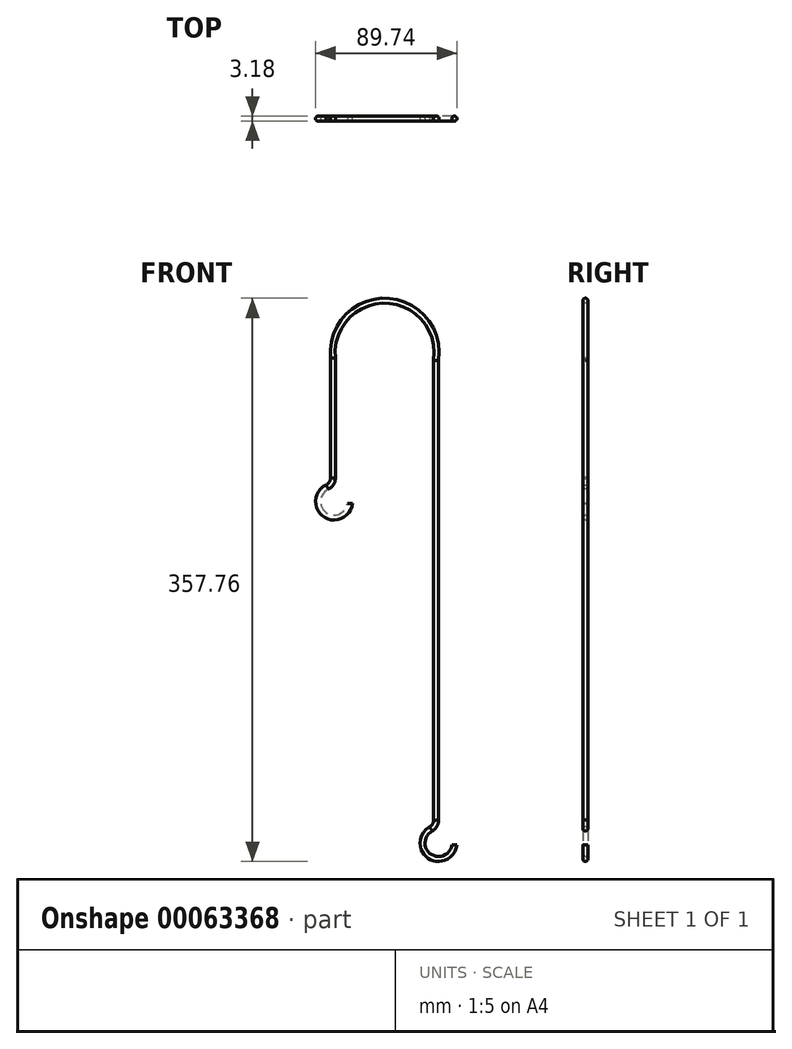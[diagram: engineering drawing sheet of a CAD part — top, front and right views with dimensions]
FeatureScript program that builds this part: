
annotation { "Feature Type Name" : "Feature", "Feature Type Description" : "" }
export const myFeature = defineFeature(function(context is Context, id is Id, definition is map)
    precondition{}
    {
        {
            var Q0;
            Q0=qCreatedBy(makeId("Front.planeOp"),FACE);
            var sketch = newSketch(context, id + "F0", { "sketchPlane" : qUnion([Q0])});
            skLineSegment(sketch, "E0", {"start": v(-32.84, 68.58) * mm, "end": v(-32.84, -7.62) * mm});
            skArc(sketch, "E1", {"start": v(32.66, 67.11) * mm, "mid": v(0.74, 105) * mm, "end": v(-32.84, 68.58) * mm});
            skLineSegment(sketch, "E2", {"start": v(32.66, 67.11) * mm, "end": v(32.66, -224.94) * mm});
            skArc(sketch, "E3", {"start": v(-36.48, -13.36) * mm, "mid": v(-38.06, -30.78) * mm, "end": v(-22.04, -23.75) * mm});
            skArc(sketch, "E4", {"start": v(29.34, -230.51) * mm, "mid": v(28.47, -247.82) * mm, "end": v(44.28, -240.74) * mm});
            skPoint(sketch, "E5.visualSharp", {"position": v(-32.84, -12.4) * mm});
            skArc(sketch, "E5.filletArc", {"start": v(-36.48, -13.36) * mm, "mid": v(-33.83, -11.01) * mm, "end": v(-32.84, -7.62) * mm});
            skPoint(sketch, "E6.visualSharp", {"position": v(32.66, -229.4) * mm});
            skArc(sketch, "E6.filletArc", {"start": v(29.34, -230.51) * mm, "mid": v(31.77, -228.18) * mm, "end": v(32.66, -224.94) * mm});
            skPoint(sketch, "E7", {"position": v(0, 105.02) * mm});
            skSolve(sketch);
        }
        {
            var Q0;
            Q0=sQuery(id+"F0.wireOp",VERTEX,"E3.end");
            var Q1;
            Q1=qCreatedBy(makeId("Top.planeOp"),FACE);
            cPlane(context, id + "F1", {"entities" : qUnion([Q0, Q1]), "cplaneType" : CPlaneType.PLANE_POINT, "offset" : 152.4 * mm, "width" : 152.4 * mm, "height" : 152.4 * mm});
        }
        {
            var Q0;
            Q0=qCreatedBy(id+"F1.planeOp",FACE);
            var sketch = newSketch(context, id + "F2", { "sketchPlane" : qUnion([Q0])});
            skCircle(sketch, "E8", {"center": v(-22.04, 0) * mm, "radius": 1.59 * mm});
            skSolve(sketch);
        }
        {
            var Q0;
            Q0 = qSketchRegion(id + "F2", true);
            var Q1;
            Q1 = qConstructionFilter(qBodyType(qCreatedBy(id + "F0" ,EDGE), BodyType.WIRE), ConstructionObject.NO);
            sweep(context, id + "F3", {"profiles" : qUnion([Q0]), "path" : qUnion([Q1])});
        }
        {
            var Q0;
            Q0=qCreatedBy(makeId("Top.planeOp"),FACE);
            cPlane(context, id + "F4", {"entities" : qUnion([Q0]), "cplaneType" : CPlaneType.OFFSET, "offset" : 103.42 * mm, "width" : 152.4 * mm, "height" : 152.4 * mm});
        }
        {
            var Q0;
            Q0=qCreatedBy(id+"F4.planeOp",FACE);
            var sketch = newSketch(context, id + "F5", { "sketchPlane" : qUnion([Q0])});
            skCircle(sketch, "E9", {"center": v(0, 0) * mm, "radius": 0.93 * mm});
            skSolve(sketch);
        }
        {
            var Q0;
            Q0=qCreatedBy(id+"F1.planeOp",FACE);
            cPlane(context, id + "F6", {"entities" : qUnion([Q0]), "cplaneType" : CPlaneType.OFFSET, "offset" : 6.35 * mm, "oppositeDirection" : true, "width" : 152.4 * mm, "height" : 152.4 * mm});
        }
        {
            var Q0;
            Q0=qCreatedBy(id+"F6.planeOp",FACE);
            var sketch = newSketch(context, id + "F7", { "sketchPlane" : qUnion([Q0])});
            skFitSpline(sketch, "E10", {"points": [v(29.34, -1.59) * mm, v(26.41, -1.59) * mm, v(24.93, -1.59) * mm, v(24.9, -1.59) * mm, v(24.63, -1.59) * mm, v(24.36, -1.59) * mm, v(24.08, -1.59) * mm, v(24.06, -1.59) * mm, v(24.04, -1.59) * mm, v(24.04, -1.59) * mm, v(23.9, -1.59) * mm, v(23.78, -1.57) * mm, v(23.65, -1.54) * mm, v(23.52, -1.5) * mm, v(23.39, -1.45) * mm, v(23.27, -1.38) * mm, v(23.15, -1.31) * mm, v(23.04, -1.23) * mm, v(22.94, -1.13) * mm, v(22.84, -1.03) * mm, v(22.75, -0.92) * mm, v(22.68, -0.8) * mm, v(22.61, -0.68) * mm, v(22.56, -0.55) * mm, v(22.52, -0.42) * mm, v(22.49, -0.28) * mm, v(22.47, -0.15) * mm, v(22.47, 0) * mm, v(22.47, 0.13) * mm, v(22.48, 0.27) * mm, v(22.52, 0.4) * mm, v(22.56, 0.54) * mm, v(22.6, 0.67) * mm, v(22.68, 0.8) * mm, v(22.75, 0.91) * mm, v(22.83, 1.02) * mm, v(22.93, 1.12) * mm, v(23.03, 1.22) * mm, v(23.14, 1.3) * mm, v(23.26, 1.38) * mm, v(23.38, 1.45) * mm, v(23.5, 1.5) * mm, v(23.64, 1.53) * mm, v(23.77, 1.57) * mm, v(23.9, 1.59) * mm, v(24.03, 1.59) * mm, v(24.04, 1.59) * mm, v(24.05, 1.59) * mm, v(24.08, 1.59) * mm, v(24.36, 1.59) * mm, v(24.63, 1.59) * mm, v(24.9, 1.59) * mm, v(26.39, 1.59) * mm, v(27.87, 1.59) * mm, v(29.34, 1.59) * mm], "construction": true});
            skFitSpline(sketch, "E11", {"points": [v(29.34, -1.59) * mm, v(26.41, -1.59) * mm, v(24.93, -1.59) * mm, v(24.9, -1.59) * mm, v(24.63, -1.59) * mm, v(24.36, -1.59) * mm, v(24.08, -1.59) * mm, v(24.06, -1.59) * mm, v(24.04, -1.59) * mm, v(24.04, -1.59) * mm, v(23.9, -1.59) * mm, v(23.78, -1.57) * mm, v(23.65, -1.54) * mm, v(23.52, -1.5) * mm, v(23.39, -1.45) * mm, v(23.27, -1.38) * mm, v(23.15, -1.31) * mm, v(23.04, -1.23) * mm, v(22.94, -1.13) * mm, v(22.84, -1.03) * mm, v(22.75, -0.92) * mm, v(22.68, -0.8) * mm, v(22.61, -0.68) * mm, v(22.56, -0.55) * mm, v(22.52, -0.42) * mm, v(22.49, -0.28) * mm, v(22.47, -0.15) * mm, v(22.47, 0) * mm, v(22.47, 0.13) * mm, v(22.48, 0.27) * mm, v(22.52, 0.4) * mm, v(22.56, 0.54) * mm, v(22.6, 0.67) * mm, v(22.68, 0.8) * mm, v(22.75, 0.91) * mm, v(22.83, 1.02) * mm, v(22.93, 1.12) * mm, v(23.03, 1.22) * mm, v(23.14, 1.3) * mm, v(23.26, 1.38) * mm, v(23.38, 1.45) * mm, v(23.5, 1.5) * mm, v(23.64, 1.53) * mm, v(23.77, 1.57) * mm, v(23.9, 1.59) * mm, v(24.03, 1.59) * mm, v(24.04, 1.59) * mm, v(24.05, 1.59) * mm, v(24.08, 1.59) * mm, v(24.36, 1.59) * mm, v(24.63, 1.59) * mm, v(24.9, 1.59) * mm, v(26.39, 1.59) * mm, v(27.87, 1.59) * mm, v(29.34, 1.59) * mm], "construction": true});
            skFitSpline(sketch, "E12", {"points": [v(29.34, -1.59) * mm, v(26.41, -1.59) * mm, v(24.93, -1.59) * mm, v(24.9, -1.59) * mm, v(24.63, -1.59) * mm, v(24.36, -1.59) * mm, v(24.08, -1.59) * mm, v(24.06, -1.59) * mm, v(24.04, -1.59) * mm, v(24.04, -1.59) * mm, v(23.9, -1.59) * mm, v(23.78, -1.57) * mm, v(23.65, -1.54) * mm, v(23.52, -1.5) * mm, v(23.39, -1.45) * mm, v(23.27, -1.38) * mm, v(23.15, -1.31) * mm, v(23.04, -1.23) * mm, v(22.94, -1.13) * mm, v(22.84, -1.03) * mm, v(22.75, -0.92) * mm, v(22.68, -0.8) * mm, v(22.61, -0.68) * mm, v(22.56, -0.55) * mm, v(22.52, -0.42) * mm, v(22.49, -0.28) * mm, v(22.47, -0.15) * mm, v(22.47, 0) * mm, v(22.47, 0.13) * mm, v(22.48, 0.27) * mm, v(22.52, 0.4) * mm, v(22.56, 0.54) * mm, v(22.6, 0.67) * mm, v(22.68, 0.8) * mm, v(22.75, 0.91) * mm, v(22.83, 1.02) * mm, v(22.93, 1.12) * mm, v(23.03, 1.22) * mm, v(23.14, 1.3) * mm, v(23.26, 1.38) * mm, v(23.38, 1.45) * mm, v(23.5, 1.5) * mm, v(23.64, 1.53) * mm, v(23.77, 1.57) * mm, v(23.9, 1.59) * mm, v(24.03, 1.59) * mm, v(24.04, 1.59) * mm, v(24.05, 1.59) * mm, v(24.08, 1.59) * mm, v(24.36, 1.59) * mm, v(24.63, 1.59) * mm, v(24.9, 1.59) * mm, v(26.39, 1.59) * mm, v(27.87, 1.59) * mm, v(29.34, 1.59) * mm], "construction": true});
            skEllipse(sketch, "E13.0", {"center": v(44.28, 0) * mm, "majorRadius": 1.59 * mm, "minorRadius": 1.59 * mm, "majorAxis": v(0, 1), "construction": true});
            skLineSegment(sketch, "E14", {"start": v(22.47, 0) * mm, "end": v(45.87, 0) * mm, "construction": true});
            skCircle(sketch, "E15", {"center": v(34.17, 0) * mm, "radius": 1.37 * mm, "construction": true});
            skCircle(sketch, "E16.0", {"center": v(-22.04, 0) * mm, "radius": 1.59 * mm, "construction": true});
            skCircle(sketch, "E17", {"center": v(-32.23, 0) * mm, "radius": 1.81 * mm, "construction": true});
            skSolve(sketch);
        }
    });
